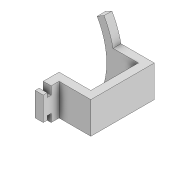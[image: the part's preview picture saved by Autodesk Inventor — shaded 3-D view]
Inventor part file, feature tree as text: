
AUTODESK INVENTOR PART (.ipt)
format: ipt  version: 2020 (Build 240168000, 168)  size: 153,600 bytes
history: native  units: mm
features: extrude x4, sketch x4
ambient origin geometry x8: Origin, YZ Plane, XZ Plane, XY Plane, X Axis, Y Axis, Z Axis, Center Point
bodies: Volumenkörper1 (feature_tree)
feature tree (8):
  extrude  "Extrusion1"  Depth=20.0mm
  extrude  "Extrusion3"  Depth=5.0mm
  extrude  "Extrusion4"  TaperAngle=90.0deg  [1 undecoded]
  extrude  "Extrusion5"  Depth=10.0mm TaperAngle=0.0deg
  sketch  "Skizze1"  dims[d0=30.0mm d1=20.0mm]
  sketch  "Skizze3"  dims[d2=5.0mm d3=5.0mm]
  sketch  "Skizze4"  dims[d4=20.0mm d5=90.0deg]
  sketch  "Skizze5"  dims[d6=40.0mm d7=10.0mm d8=0.0mm d12=10.0mm d13=10.0mm d14=10.0mm d15=60.0mm d16=50.0mm d17=60.0mm d18=17.75mm d19=0.0mm d20=200.0mm d21=180.0mm d22=30.0deg d23=30.0deg d24=40.0mm d25=20.0mm d26=15.25mm d27=0.0mm d28=20.25mm d29=0.0mm d30=140.0mm]
note: 1 required parameter value undecoded (feature->parameter linkage not recoverable at this tier; creation-order binding heuristic only, values carry confidence <= 0.55)
